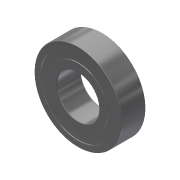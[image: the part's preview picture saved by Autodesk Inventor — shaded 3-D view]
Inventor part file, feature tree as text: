
AUTODESK INVENTOR PART (.ipt)
format: ipt  version: 2015 (Build 190159000, 159)  size: 148,480 bytes
history: native  units: in
note: dims shown in document units (in); Inventor stores cm internally (conversion verified against a paired STEP export)
features: fillet x1, other x1, imported_body x1
ambient origin geometry x8: Origin, YZ Plane, XZ Plane, XY Plane, X Axis, Y Axis, Z Axis, Center Point
bodies: Body1 (feature_tree)
feature tree (3):
  fillet  "Fillet1"  [1 undecoded]
  other  "217-4270-STEP-201410221"
  imported_body  "Base1"
note: 1 required parameter value undecoded (feature->parameter linkage not recoverable at this tier; creation-order binding heuristic only, values carry confidence <= 0.55)
